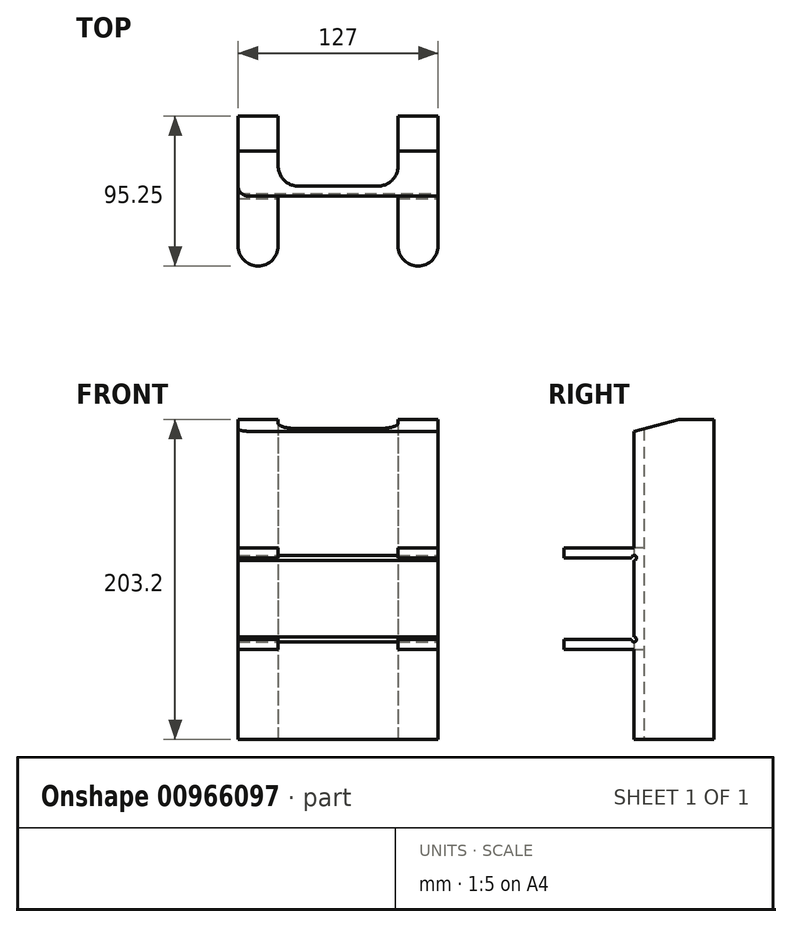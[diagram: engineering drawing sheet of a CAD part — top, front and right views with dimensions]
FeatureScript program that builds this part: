
annotation { "Feature Type Name" : "Feature", "Feature Type Description" : "" }
export const myFeature = defineFeature(function(context is Context, id is Id, definition is map)
    precondition{}
    {
        {
            var Q0;
            Q0=qCreatedBy(makeId("Top.planeOp"),FACE);
            var sketch = newSketch(context, id + "F0", { "sketchPlane" : qUnion([Q0])});
            skLineSegment(sketch, "E0", {"start": v(0, 0) * mm, "end": v(-38.1, 0) * mm});
            skLineSegment(sketch, "E1", {"start": v(-38.1, 6.35) * mm, "end": v(-38.1, 50.8) * mm});
            skLineSegment(sketch, "E2", {"start": v(-38.1, 50.8) * mm, "end": v(-63.5, 50.8) * mm});
            skLineSegment(sketch, "E3", {"start": v(-63.5, 50.8) * mm, "end": v(-63.5, -44.45) * mm});
            skLineSegment(sketch, "E4", {"start": v(-63.5, -44.45) * mm, "end": v(-38.1, -44.45) * mm});
            skLineSegment(sketch, "E5", {"start": v(-38.1, -44.45) * mm, "end": v(-38.1, -44.45) * mm});
            skLineSegment(sketch, "E6", {"start": v(-38.1, 6.35) * mm, "end": v(0, 6.35) * mm});
            skLineSegment(sketch, "E7", {"start": v(-38.1, -44.45) * mm, "end": v(-38.1, 0) * mm});
            skLineSegment(sketch, "E8", {"start": v(0, 0) * mm, "end": v(0, 50.8) * mm, "construction": true});
            skLineSegment(sketch, "E9.MirrorCS", {"start": v(38.1, 6.35) * mm, "end": v(38.1, 50.8) * mm});
            skLineSegment(sketch, "E10.MirrorCS", {"start": v(38.1, 50.8) * mm, "end": v(63.5, 50.8) * mm});
            skLineSegment(sketch, "E11.MirrorCS", {"start": v(63.5, -44.45) * mm, "end": v(38.1, -44.45) * mm});
            skLineSegment(sketch, "E12.MirrorCS", {"start": v(38.1, -44.45) * mm, "end": v(38.1, 0) * mm});
            skLineSegment(sketch, "E13.MirrorCS", {"start": v(38.1, 6.35) * mm, "end": v(0, 6.35) * mm});
            skLineSegment(sketch, "E14.MirrorCS", {"start": v(0, 0) * mm, "end": v(38.1, 0) * mm});
            skLineSegment(sketch, "E15.MirrorCS", {"start": v(63.5, 50.8) * mm, "end": v(63.5, -44.45) * mm});
            skPoint(sketch, "E16.orphan", {"position": v(38.1, 0) * mm});
            skPoint(sketch, "E17.orphan", {"position": v(38.1, 6.35) * mm});
            skSolve(sketch);
        }
        {
            var Q0;
            Q0=makeQuery(id+"F0.imprint","IMPRINT",FACE,{"disambiguationData":[TD([[makeQuery(id+"F0.imprint","IMPRINT",EDGE,{"derivedFrom":sQuery(id+"F0.wireOp",EDGE,"E0")}),-1.0]])]});
            extrude(context, id + "F1", {"entities" : qUnion([Q0]), "depth" : 203.2 * mm, "offsetDistance" : 25.4 * mm});
        }
        {
            var Q0;
            Q0=makeQuery(id+"F1.opExtrude","SWEPT_FACE",FACE,{"disambiguationData":[OSD([sQuery(id+"F0.wireOp",EDGE,"E15.MirrorCS")])]});
            var sketch = newSketch(context, id + "F2", { "sketchPlane" : qUnion([Q0])});
            skLineSegment(sketch, "E18.bottom", {"start": v(-44.45, 63.5) * mm, "end": v(0, 63.5) * mm});
            skLineSegment(sketch, "E18.top", {"start": v(-44.45, 115.32) * mm, "end": v(0, 115.32) * mm});
            skLineSegment(sketch, "E18.left", {"start": v(-44.45, 63.5) * mm, "end": v(-44.45, 115.32) * mm});
            skLineSegment(sketch, "E18.right", {"start": v(0, 63.5) * mm, "end": v(0, 115.32) * mm});
            skLineSegment(sketch, "E19", {"start": v(-44.45, 57.15) * mm, "end": v(6.35, 57.15) * mm});
            skLineSegment(sketch, "E20", {"start": v(6.35, 57.15) * mm, "end": v(6.35, 121.67) * mm});
            skLineSegment(sketch, "E21", {"start": v(6.35, 121.67) * mm, "end": v(-44.45, 121.67) * mm});
            skLineSegment(sketch, "E22", {"start": v(0, 115.32) * mm, "end": v(0, 203.2) * mm});
            skLineSegment(sketch, "E23", {"start": v(0, 63.5) * mm, "end": v(0, 0) * mm});
            skCircle(sketch, "E24", {"center": v(0, 115.32) * mm, "radius": 1.59 * mm});
            skCircle(sketch, "E25", {"center": v(0, 63.5) * mm, "radius": 1.59 * mm});
            skLineSegment(sketch, "E26", {"start": v(-44.45, 184.15) * mm, "end": v(28.58, 203.2) * mm});
            skSolve(sketch);
        }
        {
            var Q0;
            Q0=makeQuery(id+"F2.imprint","IMPRINT",FACE,{"disambiguationData":[TD([[makeQuery(id+"F2.imprint","IMPRINT",EDGE,{"derivedFrom":sQuery(id+"F2.wireOp",EDGE,"E18.bottom")}),1.0]])]});
            var Q1;
            {var subQ1=sQuery(id+"F0.wireOp",EDGE,"E15.MirrorCS");var subQ4=sQuery(id+"F2.wireOp",EDGE,"E23");var subQ6=makeQuery(id+"F1.opExtrude","CAP_EDGE",EDGE,{"disambiguationData":[OSD([subQ1])],"isStart":true});var subQ8=makeQuery(id+"F2.imprint","INTERSECT",VERTEX,{"derivedFrom":[subQ6,subQ4]});Q1=makeQuery(id+"F2.imprint","IMPRINT",FACE,{"disambiguationData":[TD([[makeQuery(id+"F2.imprint","IMPRINT",EDGE,{"disambiguationData":[TD([[subQ8,1.0]])],"derivedFrom":subQ4}),-1.0]])]});}
            var Q2;
            {var subQ1=sQuery(id+"F0.wireOp",EDGE,"E15.MirrorCS");var subQ4=sQuery(id+"F2.wireOp",EDGE,"E22");var subQ6=makeQuery(id+"F1.opExtrude","CAP_EDGE",EDGE,{"disambiguationData":[OSD([subQ1])],"isStart":false});var subQ7=makeQuery(id+"F2.imprint","INTERSECT",VERTEX,{"derivedFrom":[subQ6,subQ4]});Q2=makeQuery(id+"F2.imprint","IMPRINT",FACE,{"disambiguationData":[TD([[makeQuery(id+"F2.imprint","IMPRINT",EDGE,{"disambiguationData":[TD([[subQ7,1.0]])],"derivedFrom":subQ4}),1.0]])]});}
            var Q3;
            {var subQ5=sQuery(id+"F2.wireOp",EDGE,"E18.left");Q3=makeQuery(id+"F2.imprint","IMPRINT",FACE,{"disambiguationData":[TD([[makeQuery(id+"F2.imprint","IMPRINT",EDGE,{"derivedFrom":subQ5}),1.0]])]});}
            var Q4;
            {var subQ1=sQuery(id+"F2.wireOp",EDGE,"E18.right");var subQ3=sQuery(id+"F2.wireOp",EDGE,"E24");var subQ4=makeQuery(id+"F2.imprint","INTERSECT",VERTEX,{"derivedFrom":[subQ1,subQ3]});Q4=makeQuery(id+"F2.imprint","IMPRINT",FACE,{"disambiguationData":[TD([[makeQuery(id+"F2.imprint","IMPRINT",EDGE,{"disambiguationData":[TD([[subQ4,-1.0]])],"derivedFrom":subQ3}),1.0]])]});}
            var Q5;
            {var subQ1=sQuery(id+"F2.wireOp",EDGE,"E18.top");var subQ3=sQuery(id+"F2.wireOp",EDGE,"E24");var subQ4=makeQuery(id+"F2.imprint","INTERSECT",VERTEX,{"derivedFrom":[subQ1,subQ3]});Q5=makeQuery(id+"F2.imprint","IMPRINT",FACE,{"disambiguationData":[TD([[makeQuery(id+"F2.imprint","IMPRINT",EDGE,{"disambiguationData":[TD([[subQ4,1.0]])],"derivedFrom":subQ3}),1.0]])]});}
            var Q6;
            {var subQ1=sQuery(id+"F2.wireOp",EDGE,"E18.top");var subQ3=sQuery(id+"F2.wireOp",EDGE,"E24");var subQ4=makeQuery(id+"F2.imprint","INTERSECT",VERTEX,{"derivedFrom":[subQ1,subQ3]});Q6=makeQuery(id+"F2.imprint","IMPRINT",FACE,{"disambiguationData":[TD([[makeQuery(id+"F2.imprint","IMPRINT",EDGE,{"disambiguationData":[TD([[subQ4,-1.0]])],"derivedFrom":subQ3}),1.0]])]});}
            var Q7;
            {var subQ1=sQuery(id+"F2.wireOp",EDGE,"E18.right");var subQ3=sQuery(id+"F2.wireOp",EDGE,"E25");var subQ4=makeQuery(id+"F2.imprint","INTERSECT",VERTEX,{"derivedFrom":[subQ1,subQ3]});Q7=makeQuery(id+"F2.imprint","IMPRINT",FACE,{"disambiguationData":[TD([[makeQuery(id+"F2.imprint","IMPRINT",EDGE,{"disambiguationData":[TD([[subQ4,1.0]])],"derivedFrom":subQ3}),1.0]])]});}
            var Q8;
            {var subQ1=sQuery(id+"F2.wireOp",EDGE,"E18.bottom");var subQ3=sQuery(id+"F2.wireOp",EDGE,"E25");var subQ4=makeQuery(id+"F2.imprint","INTERSECT",VERTEX,{"derivedFrom":[subQ1,subQ3]});Q8=makeQuery(id+"F2.imprint","IMPRINT",FACE,{"disambiguationData":[TD([[makeQuery(id+"F2.imprint","IMPRINT",EDGE,{"disambiguationData":[TD([[subQ4,-1.0]])],"derivedFrom":subQ3}),1.0]])]});}
            var Q9;
            {var subQ0=sQuery(id+"F2.wireOp",EDGE,"E22");var subQ1=makeQuery(id+"F1.opExtrude","CAP_EDGE",EDGE,{"disambiguationData":[OSD([sQuery(id+"F0.wireOp",EDGE,"E15.MirrorCS")])],"isStart":false});var subQ2=makeQuery(id+"F2.imprint","INTERSECT",VERTEX,{"derivedFrom":[subQ1,subQ0]});Q9=makeQuery(id+"F2.imprint","IMPRINT",FACE,{"disambiguationData":[TD([[makeQuery(id+"F2.imprint","IMPRINT",EDGE,{"disambiguationData":[TD([[subQ2,1.0]])],"derivedFrom":subQ0}),-1.0]])]});}
            var Q10;
            {var subQ0=sQuery(id+"F2.wireOp",EDGE,"E21");var subQ3=sQuery(id+"F2.wireOp",EDGE,"E22");var subQ4=makeQuery(id+"F2.imprint","INTERSECT",VERTEX,{"derivedFrom":[subQ0,subQ3]});Q10=makeQuery(id+"F2.imprint","IMPRINT",FACE,{"disambiguationData":[TD([[makeQuery(id+"F2.imprint","IMPRINT",EDGE,{"disambiguationData":[TD([[subQ4,-1.0]])],"derivedFrom":subQ3}),1.0]])]});}
            extrude(context, id + "F3", {"entities" : qUnion([Q0, Q1, Q2, Q3, Q4, Q5, Q6, Q7, Q8, Q9, Q10]), "operationType" : NewBodyOperationType.REMOVE, "endBound" : BoundingType.THROUGH_ALL, "oppositeDirection" : true, "depth" : 25.4 * mm, "offsetDistance" : 25.4 * mm});
        }
        {
            var Q0;
            {var subQ0=sQuery(id+"F0.wireOp",EDGE,"E11.MirrorCS");var subQ1=sQuery(id+"F0.wireOp",EDGE,"E12.MirrorCS");Q0=makeQuery(id+"F3.boolean.opBoolean","SPLIT",EDGE,{"disambiguationData":[TD([makeQuery(id+"F3.opExtrude","SWEPT_FACE",FACE,{"disambiguationData":[OSD([sQuery(id+"F2.wireOp",EDGE,"E18.top")])]})])],"derivedFrom":makeQuery(id+"F1.opExtrude","SWEPT_EDGE",EDGE,{"disambiguationData":[OSD([subQ0,subQ1])]})});}
            var Q1;
            {var subQ0=sQuery(id+"F0.wireOp",EDGE,"E11.MirrorCS");var subQ1=sQuery(id+"F0.wireOp",EDGE,"E15.MirrorCS");Q1=makeQuery(id+"F3.boolean.opBoolean","SPLIT",EDGE,{"disambiguationData":[TD([makeQuery(id+"F3.opExtrude","SWEPT_FACE",FACE,{"disambiguationData":[OSD([sQuery(id+"F2.wireOp",EDGE,"E18.top")])]})])],"derivedFrom":makeQuery(id+"F1.opExtrude","SWEPT_EDGE",EDGE,{"disambiguationData":[OSD([subQ0,subQ1])]})});}
            var Q2;
            {var subQ0=sQuery(id+"F0.wireOp",EDGE,"E3");var subQ1=sQuery(id+"F0.wireOp",EDGE,"E4");Q2=makeQuery(id+"F3.boolean.opBoolean","SPLIT",EDGE,{"disambiguationData":[TD([makeQuery(id+"F3.opExtrude","SWEPT_FACE",FACE,{"disambiguationData":[OSD([sQuery(id+"F2.wireOp",EDGE,"E18.top")])]})])],"derivedFrom":makeQuery(id+"F1.opExtrude","SWEPT_EDGE",EDGE,{"disambiguationData":[OSD([subQ0,subQ1])]})});}
            var Q3;
            {var subQ0=sQuery(id+"F0.wireOp",EDGE,"E4");var subQ1=sQuery(id+"F0.wireOp",EDGE,"E7");Q3=makeQuery(id+"F3.boolean.opBoolean","SPLIT",EDGE,{"disambiguationData":[TD([makeQuery(id+"F3.opExtrude","SWEPT_FACE",FACE,{"disambiguationData":[OSD([sQuery(id+"F2.wireOp",EDGE,"E18.top")])]})])],"derivedFrom":makeQuery(id+"F1.opExtrude","SWEPT_EDGE",EDGE,{"disambiguationData":[OSD([subQ0,subQ1])]})});}
            var Q4;
            {var subQ0=sQuery(id+"F0.wireOp",EDGE,"E4");var subQ1=sQuery(id+"F0.wireOp",EDGE,"E7");Q4=makeQuery(id+"F3.boolean.opBoolean","SPLIT",EDGE,{"disambiguationData":[TD([makeQuery(id+"F3.opExtrude","SWEPT_FACE",FACE,{"disambiguationData":[OSD([sQuery(id+"F2.wireOp",EDGE,"E18.bottom")])]})])],"derivedFrom":makeQuery(id+"F1.opExtrude","SWEPT_EDGE",EDGE,{"disambiguationData":[OSD([subQ0,subQ1])]})});}
            var Q5;
            {var subQ0=sQuery(id+"F0.wireOp",EDGE,"E3");var subQ1=sQuery(id+"F0.wireOp",EDGE,"E4");Q5=makeQuery(id+"F3.boolean.opBoolean","SPLIT",EDGE,{"disambiguationData":[TD([makeQuery(id+"F3.opExtrude","SWEPT_FACE",FACE,{"disambiguationData":[OSD([sQuery(id+"F2.wireOp",EDGE,"E18.bottom")])]})])],"derivedFrom":makeQuery(id+"F1.opExtrude","SWEPT_EDGE",EDGE,{"disambiguationData":[OSD([subQ0,subQ1])]})});}
            var Q6;
            {var subQ0=sQuery(id+"F0.wireOp",EDGE,"E11.MirrorCS");var subQ1=sQuery(id+"F0.wireOp",EDGE,"E12.MirrorCS");Q6=makeQuery(id+"F3.boolean.opBoolean","SPLIT",EDGE,{"disambiguationData":[TD([makeQuery(id+"F3.opExtrude","SWEPT_FACE",FACE,{"disambiguationData":[OSD([sQuery(id+"F2.wireOp",EDGE,"E18.bottom")])]})])],"derivedFrom":makeQuery(id+"F1.opExtrude","SWEPT_EDGE",EDGE,{"disambiguationData":[OSD([subQ0,subQ1])]})});}
            var Q7;
            {var subQ0=sQuery(id+"F0.wireOp",EDGE,"E11.MirrorCS");var subQ1=sQuery(id+"F0.wireOp",EDGE,"E15.MirrorCS");Q7=makeQuery(id+"F3.boolean.opBoolean","SPLIT",EDGE,{"disambiguationData":[TD([makeQuery(id+"F3.opExtrude","SWEPT_FACE",FACE,{"disambiguationData":[OSD([sQuery(id+"F2.wireOp",EDGE,"E18.bottom")])]})])],"derivedFrom":makeQuery(id+"F1.opExtrude","SWEPT_EDGE",EDGE,{"disambiguationData":[OSD([subQ0,subQ1])]})});}
            fillet(context, id + "F4", {"entities" : qUnion([Q0, Q1, Q2, Q3, Q4, Q5, Q6, Q7]), "radius" : 12.7 * mm, "tangentPropagation" : true, "allowEdgeOverflow" : false});
        }
        {
            var Q0;
            Q0=makeQuery(id+"F3.boolean.opBoolean","COPY",EDGE,{"derivedFrom":makeQuery(id+"F3.opExtrude","CAP_EDGE",EDGE,{"disambiguationData":[OSD([sQuery(id+"F2.wireOp",EDGE,"E22")])],"isStart":true})});
            var Q1;
            Q1=makeQuery(id+"F3.boolean.opBoolean","INTERSECT",EDGE,{"derivedFrom":[makeQuery(id+"F1.opExtrude","SWEPT_FACE",FACE,{"disambiguationData":[OSD([sQuery(id+"F0.wireOp",EDGE,"E3")])]}),makeQuery(id+"F3.opExtrude","SWEPT_FACE",FACE,{"disambiguationData":[OSD([sQuery(id+"F2.wireOp",EDGE,"E22")])]})]});
            fillet(context, id + "F5", {"entities" : qUnion([Q0, Q1]), "radius" : 6.35 * mm, "tangentPropagation" : true, "allowEdgeOverflow" : false});
        }
        {
            var Q0;
            Q0=makeQuery(id+"F3.boolean.opBoolean","COPY",EDGE,{"derivedFrom":makeQuery(id+"F3.opExtrude","CAP_EDGE",EDGE,{"disambiguationData":[OSD([sQuery(id+"F2.wireOp",EDGE,"E23")])],"isStart":true})});
            var Q1;
            Q1=makeQuery(id+"F3.boolean.opBoolean","INTERSECT",EDGE,{"derivedFrom":[makeQuery(id+"F1.opExtrude","SWEPT_FACE",FACE,{"disambiguationData":[OSD([sQuery(id+"F0.wireOp",EDGE,"E3")])]}),makeQuery(id+"F3.opExtrude","SWEPT_FACE",FACE,{"disambiguationData":[OSD([sQuery(id+"F2.wireOp",EDGE,"E23")])]})]});
            fillet(context, id + "F6", {"entities" : qUnion([Q0, Q1]), "radius" : 6.35 * mm, "tangentPropagation" : true, "allowEdgeOverflow" : false});
        }
        {
            var Q0;
            Q0=makeQuery(id+"F1.opExtrude","SWEPT_EDGE",EDGE,{"disambiguationData":[OSD([sQuery(id+"F0.wireOp",EDGE,"E1"),sQuery(id+"F0.wireOp",EDGE,"E6")])]});
            var Q1;
            Q1=makeQuery(id+"F1.opExtrude","SWEPT_EDGE",EDGE,{"disambiguationData":[OSD([sQuery(id+"F0.wireOp",EDGE,"E9.MirrorCS"),sQuery(id+"F0.wireOp",EDGE,"E13.MirrorCS")])]});
            fillet(context, id + "F7", {"entities" : qUnion([Q0, Q1]), "radius" : 12.7 * mm, "tangentPropagation" : true, "allowEdgeOverflow" : false});
        }
    });
